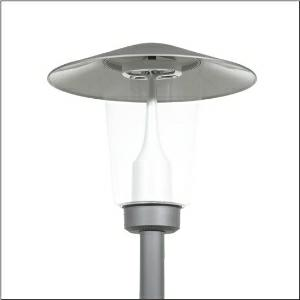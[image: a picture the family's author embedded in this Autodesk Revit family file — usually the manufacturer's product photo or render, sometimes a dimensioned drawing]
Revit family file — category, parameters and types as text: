
# Revit family: pilzleuchte_iq___p1_0a_5xa5235bf14hp_6096
name_source: partatom
category: Lighting Fixtures
units: mm (PartAtom-declared; Revit-internal decimal feet)

## family parameters
Cut with Voids When Loaded = No
Host = Face
Light Source = No
Part Type = Normal
Room Calculation Point = No
Round Connector Dimension = Use Diameter
Shared = No

## types (1)
- --- (1 x LED, 3920 lm, 33.6 W, 2200K)
    Apparent Load = 34 VA
    CIE Flux Codes = 35 64 90 96 100
    Color Rendering = 70
    Color Temperature = 2200K
    Default Elevation = 1800 mm
    Description = Mushroom Luminaire iQ, mast luminaire, Module 540 iQ-SR, primary light control with 3 zone facetted reflector, of plastic, silver coated, highly specular, structured, primary optical cover: cover, of PMMA, transparent, light distribution: P1.0a, light emission: direct distribution, primary light characteristic: strongly asymmetric, installation type: post-top, LED, High Power LED, rated luminous flux: 3.920lm, luminous efficacy: 117lm/W, light colour: 722, colour temperature: 2200K, control gear: iQ Street-Remote, control: pre-setting: logarithmic dimming characteristic, Street-Remote, Auto-Match, Temp-Guard, Lumen-Switch, Night-Set, Smart-Wire, Light-Fading, Desk-Remote (wireless, voltage-free reading and setting of iQ features in the workshop via application-optimized NFC function/RFID function), optimised constant luminous flux control (CLO 2.0), with terminal, 6-pole, max. 2.5mm², mains connection: 230..240V, AC, 50/60Hz, start of lifetime: 34W, end of service life: 36W, reduction: 15W, luminaire housing, upper part, of glass-fibre reinforced polyester, coated, Siteco® metallic grey (DB 702S), diameter: 650mm, height: 586mm, spigot size: d x l = 76 x 70mm (post-top) | with reducer (optional accessory) 60 x 70mm, mounting height: 3..5m, post-top mast mounting element, of diecast aluminium, coated, Siteco® metallic grey (DB 702S), Module 540 iQ-SR, traffic white (RAL 9016), equipment: Power, protection rating (complete): IP65, insulation class (complete): insulation class II (safety insulation), certification: CE, ENEC, VDE, packaging unit: 1 piece

Light Distribution: P1.0a
    Height = 586 mm
    Lamp = 1 x LED
    Lamp Light Flux = 3920 lm
    Lamp Power = 33.6 W
    Lamp count = 1
    Length = 650 mm
    Luminous efficacy = 117 lm/W
    Manufacturer = Siteco
    ModVariant = No
    Model = 5XA5235BF14HP
    Number of Poles = 1
    OnlyDefault = Yes
    Power Factor = 1
    Product Name = Pilzleuchte iQ | P1.0a
    Product group = mast luminaire | pylon top
    ProductGroupID = 6100
    Protection Class = Protection class II
    Protection Degree = IP 65
    RLX_Detail_Level = 1
    RLX_Emergency_Light_Flux = 0 lm
    RLX_Emergency_Type = 0
    RLX_Emergency_Type_DB = No
    RlxData = <blob elided: 51909 chars, md5=24ddf05d>
    Socket = socket
    Standby Power = 0 W
    System Light Flux = 3920 lm
    System Power = 34 W
    Type Comments = factory setting: luminous flux: 100 % | dim-lin: 254 | 695 mA
    Type Image = l_1006077.jpg
    URL = http://relux.com
    VarID = @adj_189647
    Voltage = 0 V
    Weight = 0.00 kg
    Width = 0 mm  [stored 0 ft]

note: [stored X ft] marks values corroborated as IEEE doubles in the binary element streams (Revit-internal decimal feet)

## geometry (parser evidence)
native form markers: Blend x4, Sweep x11
no freeform markers — native parametric forms only
